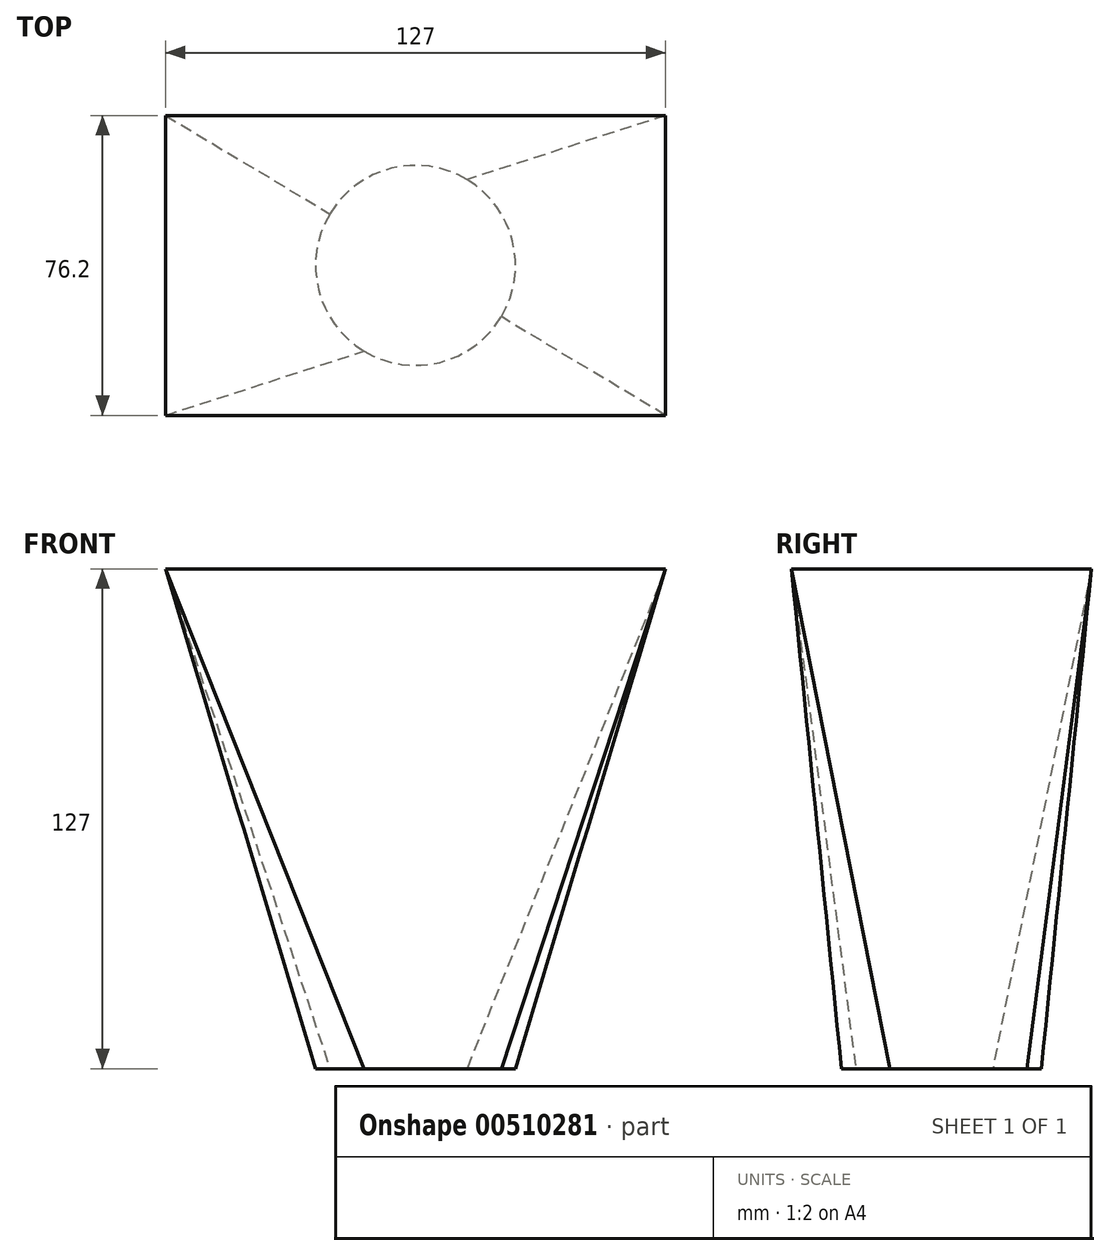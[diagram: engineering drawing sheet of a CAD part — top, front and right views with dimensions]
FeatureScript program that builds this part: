
annotation { "Feature Type Name" : "Feature", "Feature Type Description" : "" }
export const myFeature = defineFeature(function(context is Context, id is Id, definition is map)
    precondition{}
    {
        {
            var Q0;
            Q0=qCreatedBy(makeId("Top.planeOp"),FACE);
            cPlane(context, id + "F0", {"entities" : qUnion([Q0]), "cplaneType" : CPlaneType.OFFSET, "offset" : 127 * mm, "width" : 152.4 * mm, "height" : 152.4 * mm});
        }
        {
            var Q0;
            Q0=qCreatedBy(makeId("Top.planeOp"),FACE);
            var sketch = newSketch(context, id + "F1", { "sketchPlane" : qUnion([Q0])});
            skCircle(sketch, "E0", {"center": v(0, 0) * mm, "radius": 25.4 * mm});
            skSolve(sketch);
        }
        {
            var Q0;
            Q0=qCreatedBy(id+"F0.planeOp",FACE);
            var sketch = newSketch(context, id + "F2", { "sketchPlane" : qUnion([Q0])});
            skLineSegment(sketch, "E1.bottom", {"start": v(-63.5, 38.1) * mm, "end": v(63.5, 38.1) * mm});
            skLineSegment(sketch, "E1.top", {"start": v(-63.5, -38.1) * mm, "end": v(63.5, -38.1) * mm});
            skLineSegment(sketch, "E1.left", {"start": v(-63.5, 38.1) * mm, "end": v(-63.5, -38.1) * mm});
            skLineSegment(sketch, "E1.right", {"start": v(63.5, 38.1) * mm, "end": v(63.5, -38.1) * mm});
            skPoint(sketch, "E1.middle", {"position": v(0, 0) * mm});
            skSolve(sketch);
        }
        {
            var Q0;
            Q0=makeQuery(id+"F2.imprint","IMPRINT",FACE,{"disambiguationData":[TD([[makeQuery(id+"F2.imprint","IMPRINT",EDGE,{"derivedFrom":sQuery(id+"F2.wireOp",EDGE,"E1.bottom")}),-1.0]])]});
            var Q1;
            Q1=makeQuery(id+"F1.imprint","IMPRINT",FACE,{"disambiguationData":[TD([[makeQuery(id+"F1.imprint","IMPRINT",EDGE,{"derivedFrom":sQuery(id+"F1.wireOp",EDGE,"E0")}),1.0]])]});
            loft(context, id + "F3", {"sheetProfilesArray" : [{ "sheetProfileEntities" : qUnion([Q0]) }, { "sheetProfileEntities" : qUnion([Q1]) }]});
        }
    });
